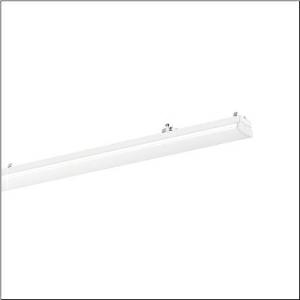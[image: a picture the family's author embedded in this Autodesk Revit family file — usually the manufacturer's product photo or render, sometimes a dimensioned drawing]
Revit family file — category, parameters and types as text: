
# Revit family: licross_11_recessed_opal_mo_51te1ddv4e5g
name_source: partatom
category: Lighting Fixtures
units: mm (PartAtom-declared; Revit-internal decimal feet)

## family parameters
Cut with Voids When Loaded = No
Host = Face
Light Source = No
Part Type = Normal
Room Calculation Point = No
Round Connector Dimension = Use Diameter
Shared = No

## types (1)
- --- (1 x LED, 14560 lm, 84.1 W, 4000K)
    Apparent Load = 84 VA
    CIE Flux Codes = 44 73 91 87 100
    Color Rendering = 80
    Color Temperature = 4000K
    Default Elevation = 1800 mm
    Description = Licross 11 recessed opal MO, luminaire insert, of sheet steel, coil coated, white, length: 2.250mm, width: 76mm, height: 87mm, LED rated luminous flux: 14.560lm, light colour: 840, SDCM (Standard Deviation of Colour Matching)MacAdam ≤ 2 SDCM (initial), control gear: DALI 2, with plug, 5-pole, with phase selection, mains connection: 220..240V, AC, 50/60Hz, rated input power: 84W, internal wiring halogen-free, primary optical cover: cover, of PMMA, light emission: direct with ceiling illumination distribution, primary light characteristic: symmetric, protection rating (complete): IP54, insulation class (complete): insulation class I (protective earthing), certification: CE, ENEC, VDE, UKCA, protection symbol: D if used in an environment with non-conductive dust loads with corresponding accessories, impact resistance: IK06, permissible ambient temperature for indoor applications: -25..+35°C, corresponds to IFS (International Featured Standards) requirements for safety and quality in the food industry, reducing of maximum allowable ambient temperature of 5°C with ceiling mounting, LABS conformity tested according to VDMA 24364:2018-05, The light source and the operating device comply with the requirements of the Ecodesign Regulation (EU) 2019/2020 and are replaceable in accordance with this regulation, packaging unit: 1 piece
    Height = 83 mm
    Lamp = 1 x LED
    Lamp Light Flux = 14560 lm
    Lamp Power = 84.1 W
    Lamp count = 1
    Length = 2250 mm
    Luminous efficacy = 173 lm/W
    Manufacturer = Siteco
    ModVariant = No
    Model = 51TE1DDV4E5G
    Mounting Place = Ceiling
    Mounting Type = Pendant
    Number of Poles = 1
    OnlyDefault = Yes
    Power Factor = 1
    Product Name = Licross 11 recessed opal MO
    Product group = luminaire insert | ceiling pendant
    ProductGroupID = 901
    Protection Class = Protection class I
    Protection Degree = IP 54
    RLX_Detail_Level = 1
    RLX_Emergency_Light_Flux = 0 lm
    RLX_Emergency_Type = 0
    RLX_Emergency_Type_DB = No
    RlxData = <blob elided: 26981 chars, md5=a1466b49>
    Socket = socket
    Standby Power = 0 W
    System Light Flux = 14560 lm
    System Power = 84 W
    Type Comments = factory setting: luminous flux: 100 % | dim-lin: 254 | 378 mA
    Type Image = l_1313666.jpg
    URL = http://relux.com
    VarID = @adj_084087
    Voltage = 0 V
    Weight = 0.00 kg
    Width = 76 mm

## geometry (parser evidence)
native form markers: Blend x4, Sweep x14
no freeform markers — native parametric forms only
